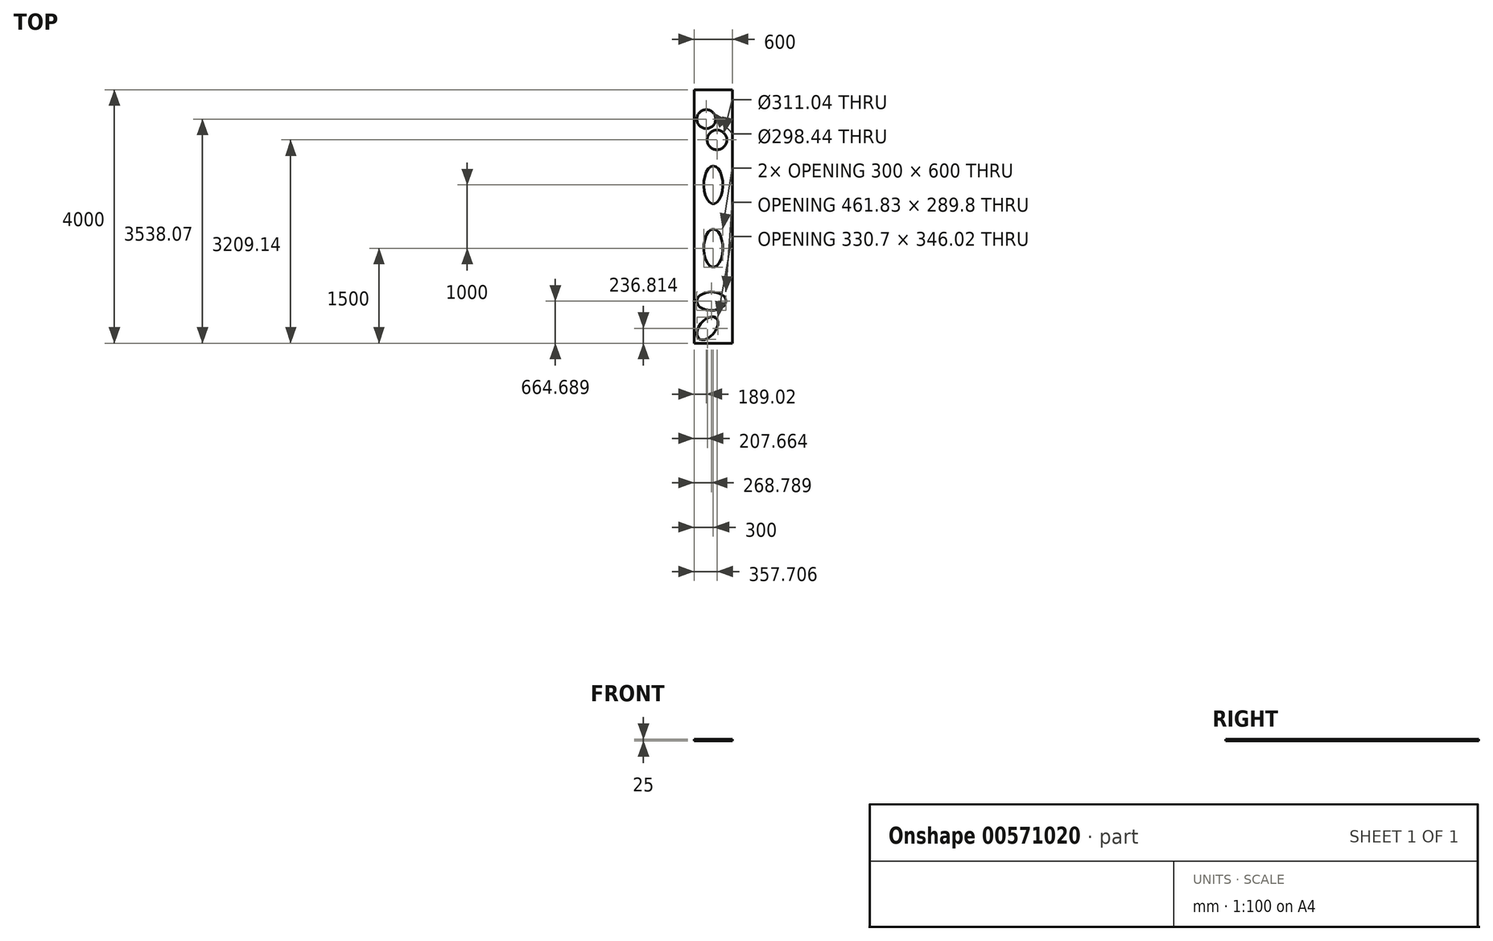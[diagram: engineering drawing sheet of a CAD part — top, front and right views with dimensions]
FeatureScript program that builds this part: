
annotation { "Feature Type Name" : "Feature", "Feature Type Description" : "" }
export const myFeature = defineFeature(function(context is Context, id is Id, definition is map)
    precondition{}
    {
        {
            var Q0;
            Q0=qCreatedBy(makeId("Top.planeOp"),FACE);
            var sketch = newSketch(context, id + "F0", { "sketchPlane" : qUnion([Q0])});
            skLineSegment(sketch, "E0.bottom", {"start": v(0, 0) * mm, "end": v(600, 0) * mm});
            skLineSegment(sketch, "E0.top", {"start": v(0, 4000) * mm, "end": v(600, 4000) * mm});
            skLineSegment(sketch, "E0.left", {"start": v(0, 0) * mm, "end": v(0, 4000) * mm});
            skLineSegment(sketch, "E0.right", {"start": v(600, 0) * mm, "end": v(600, 4000) * mm});
            skArc(sketch, "E1", {"start": v(600, 486.54) * mm, "mid": v(450, 336.54) * mm, "end": v(600, 186.54) * mm});
            skArc(sketch, "E2", {"start": v(600, 883.94) * mm, "mid": v(450, 733.94) * mm, "end": v(600, 583.94) * mm});
            skEllipse(sketch, "E3", {"center": v(300, 1500) * mm, "majorRadius": 300 * mm, "minorRadius": 150 * mm, "majorAxis": v(0, 1)});
            skPoint(sketch, "E4", {"position": v(300, 1800) * mm});
            skEllipse(sketch, "E5", {"center": v(300, 2500) * mm, "majorRadius": 300 * mm, "minorRadius": 150 * mm, "majorAxis": v(0, 1)});
            skLineSegment(sketch, "E6", {"start": v(0, 3100) * mm, "end": v(150, 3100) * mm});
            skArc(sketch, "E7", {"start": v(150, 2900) * mm, "mid": v(250, 3000) * mm, "end": v(150, 3100) * mm});
            skArc(sketch, "E8", {"start": v(150, 2900) * mm, "mid": v(79.29, 2929.29) * mm, "end": v(50, 3000) * mm});
            skLineSegment(sketch, "E9", {"start": v(50, 3000) * mm, "end": v(0, 3000) * mm});
            skSolve(sketch);
        }
        {
            var Q0;
            {var subQ4=sQuery(id+"F0.wireOp",EDGE,"E0.bottom");Q0=makeQuery(id+"F0.imprint","IMPRINT",FACE,{"disambiguationData":[TD([[makeQuery(id+"F0.imprint","IMPRINT",EDGE,{"derivedFrom":subQ4}),1.0]])]});}
            var Q1;
            {var subQ0=sQuery(id+"F0.wireOp",EDGE,"E6");Q1=makeQuery(id+"F0.imprint","IMPRINT",FACE,{"disambiguationData":[TD([[makeQuery(id+"F0.imprint","IMPRINT",EDGE,{"derivedFrom":subQ0}),-1.0]])]});}
            var Q2;
            {var subQ0=sQuery(id+"F0.wireOp",EDGE,"E2");Q2=makeQuery(id+"F0.imprint","IMPRINT",FACE,{"disambiguationData":[TD([[makeQuery(id+"F0.imprint","IMPRINT",EDGE,{"derivedFrom":subQ0}),1.0]])]});}
            var Q3;
            {var subQ0=sQuery(id+"F0.wireOp",EDGE,"E1");Q3=makeQuery(id+"F0.imprint","IMPRINT",FACE,{"disambiguationData":[TD([[makeQuery(id+"F0.imprint","IMPRINT",EDGE,{"derivedFrom":subQ0}),1.0]])]});}
            extrude(context, id + "F1", {"entities" : qUnion([Q0, Q1, Q2, Q3]), "depth" : 25 * mm, "offsetDistance" : 25 * mm});
        }
        {
            var Q0;
            Q0=makeQuery(id+"F1.opExtrude","CAP_FACE",FACE,{"disambiguationData":[OSD([sQuery(id+"F0.wireOp",EDGE,"E0.bottom"),sQuery(id+"F0.wireOp",EDGE,"E0.top"),sQuery(id+"F0.wireOp",EDGE,"E0.left"),sQuery(id+"F0.wireOp",EDGE,"E0.right"),sQuery(id+"F0.wireOp",EDGE,"E3"),sQuery(id+"F0.wireOp",EDGE,"E5")])],"isStart":false});
            var sketch = newSketch(context, id + "F2", { "sketchPlane" : qUnion([Q0])});
            skCircle(sketch, "E10", {"center": v(189.02, 3538.07) * mm, "radius": 149.22 * mm});
            skCircle(sketch, "E11", {"center": v(357.7, 3209.14) * mm, "radius": 155.52 * mm});
            skEllipse(sketch, "E12", {"center": v(268.79, 664.69) * mm, "majorRadius": 230.92 * mm, "minorRadius": 144.9 * mm, "majorAxis": v(1, 0)});
            skEllipse(sketch, "E13", {"center": v(207.66, 236.81) * mm, "majorRadius": 212.18 * mm, "minorRadius": 127.58 * mm, "majorAxis": v(0.64, 0.77)});
            skSolve(sketch);
        }
        {
            var Q0;
            Q0 = qSketchRegion(id + "F2", true);
            extrude(context, id + "F3", {"entities" : qUnion([Q0]), "operationType" : NewBodyOperationType.REMOVE, "oppositeDirection" : true, "depth" : 25 * mm, "offsetDistance" : 25 * mm});
        }
    });
